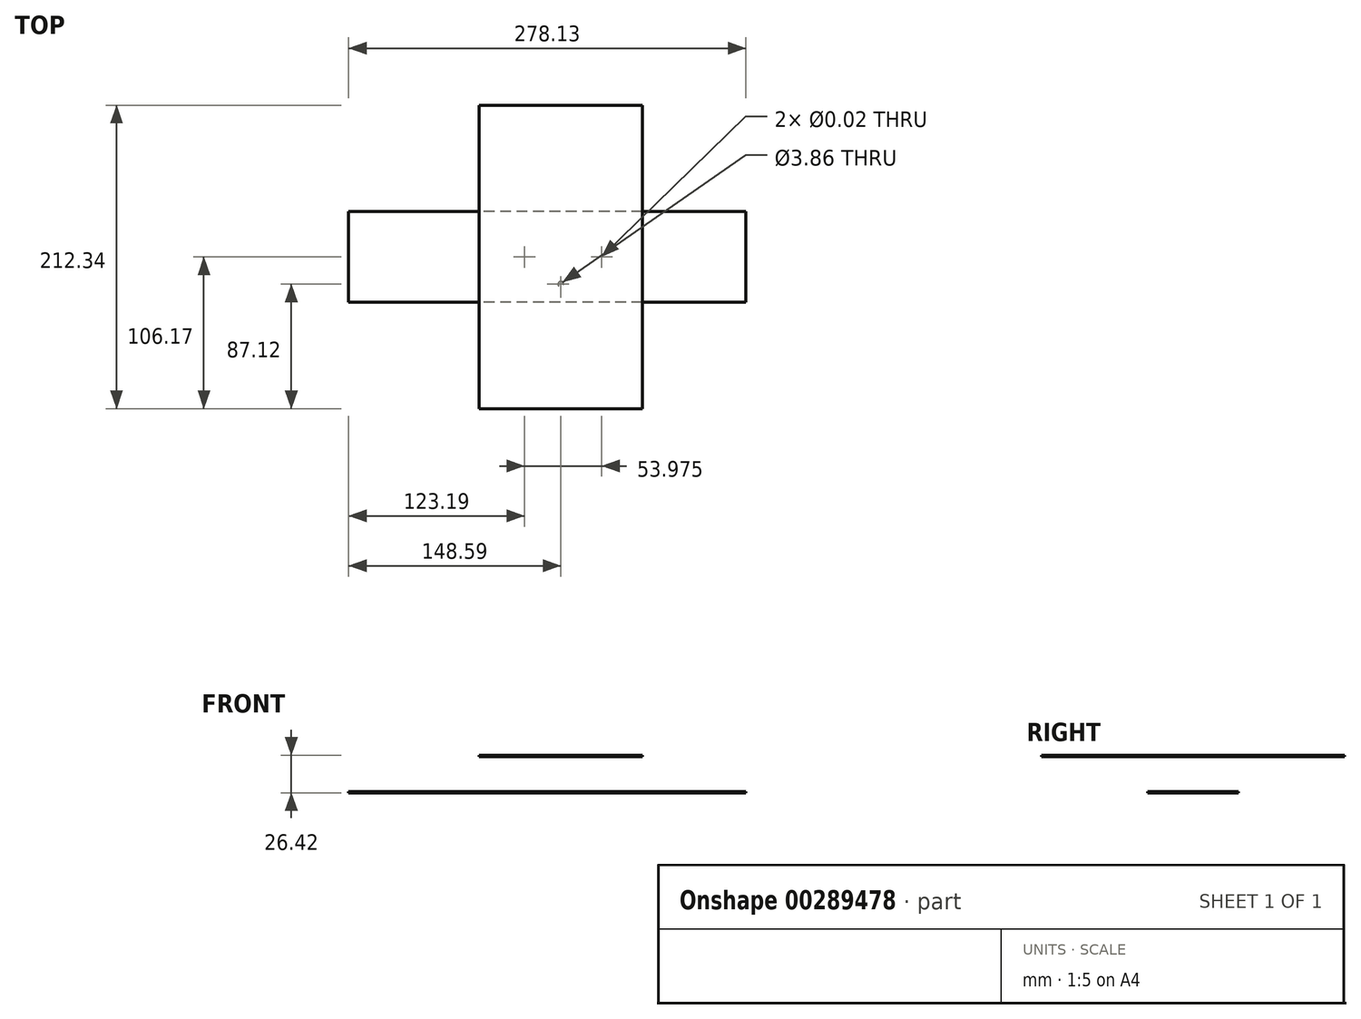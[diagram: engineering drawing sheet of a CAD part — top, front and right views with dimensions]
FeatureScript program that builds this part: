
annotation { "Feature Type Name" : "Feature", "Feature Type Description" : "" }
export const myFeature = defineFeature(function(context is Context, id is Id, definition is map)
    precondition{}
    {
        {
            var Q0;
            Q0=qCreatedBy(makeId("Top.planeOp"),FACE);
            var sketch = newSketch(context, id + "F0", { "sketchPlane" : qUnion([Q0])});
            skLineSegment(sketch, "E0.bottom", {"start": v(57.15, 31.75) * mm, "end": v(-57.15, 31.75) * mm});
            skLineSegment(sketch, "E0.top", {"start": v(57.15, -31.75) * mm, "end": v(-57.15, -31.75) * mm});
            skLineSegment(sketch, "E0.left", {"start": v(57.15, 31.75) * mm, "end": v(57.15, -31.75) * mm});
            skLineSegment(sketch, "E0.right", {"start": v(-57.15, 31.75) * mm, "end": v(-57.15, -31.75) * mm});
            skPoint(sketch, "E0.middle", {"position": v(0, 0) * mm});
            skLineSegment(sketch, "E1.bottom", {"start": v(57.15, 31.75) * mm, "end": v(97.8, 31.75) * mm});
            skLineSegment(sketch, "E1.top", {"start": v(57.15, -31.75) * mm, "end": v(97.8, -31.75) * mm});
            skLineSegment(sketch, "E1.right", {"start": v(97.8, 31.75) * mm, "end": v(97.8, -31.75) * mm});
            skLineSegment(sketch, "E2.bottom", {"start": v(97.8, 31.75) * mm, "end": v(129.54, 31.75) * mm});
            skLineSegment(sketch, "E2.top", {"start": v(97.8, -31.75) * mm, "end": v(129.54, -31.75) * mm});
            skLineSegment(sketch, "E2.right", {"start": v(129.54, 31.75) * mm, "end": v(129.54, -31.75) * mm});
            skLineSegment(sketch, "E3.bottom", {"start": v(-57.15, -31.75) * mm, "end": v(57.15, -31.75) * mm});
            skLineSegment(sketch, "E3.top", {"start": v(-57.15, -74.42) * mm, "end": v(57.15, -74.42) * mm});
            skLineSegment(sketch, "E3.left", {"start": v(-57.15, -31.75) * mm, "end": v(-57.15, -74.42) * mm});
            skLineSegment(sketch, "E3.right", {"start": v(57.15, -31.75) * mm, "end": v(57.15, -74.42) * mm});
            skLineSegment(sketch, "E4.top", {"start": v(-57.15, -106.17) * mm, "end": v(57.15, -106.17) * mm});
            skLineSegment(sketch, "E4.left", {"start": v(-57.15, -74.42) * mm, "end": v(-57.15, -106.17) * mm});
            skLineSegment(sketch, "E4.right", {"start": v(57.15, -74.42) * mm, "end": v(57.15, -106.17) * mm});
            skLineSegment(sketch, "E5.MirrorCS", {"start": v(-57.15, 31.75) * mm, "end": v(-97.8, 31.75) * mm});
            skLineSegment(sketch, "E6.MirrorCS", {"start": v(-57.15, -31.75) * mm, "end": v(-97.8, -31.75) * mm});
            skLineSegment(sketch, "E7.MirrorCS", {"start": v(-97.8, 31.75) * mm, "end": v(-97.8, -31.75) * mm});
            skLineSegment(sketch, "E8.MirrorCS", {"start": v(57.15, 74.42) * mm, "end": v(57.15, 106.17) * mm});
            skLineSegment(sketch, "E9.MirrorCS", {"start": v(-57.15, 74.42) * mm, "end": v(-57.15, 106.17) * mm});
            skLineSegment(sketch, "E10.MirrorCS", {"start": v(-57.15, 106.17) * mm, "end": v(57.15, 106.17) * mm});
            skLineSegment(sketch, "E11", {"start": v(-57.15, 74.42) * mm, "end": v(57.15, 74.42) * mm});
            skLineSegment(sketch, "E12.bottom", {"start": v(-97.8, 31.75) * mm, "end": v(-148.6, 31.75) * mm});
            skLineSegment(sketch, "E12.top", {"start": v(-97.8, -31.75) * mm, "end": v(-148.6, -31.75) * mm});
            skLineSegment(sketch, "E12.right", {"start": v(-148.6, 31.75) * mm, "end": v(-148.6, -31.75) * mm});
            skLineSegment(sketch, "E13", {"start": v(0, 0) * mm, "end": v(57.15, 0) * mm, "construction": true});
            skPoint(sketch, "E14", {"position": v(28.58, 0) * mm});
            skLineSegment(sketch, "E15", {"start": v(0, 0) * mm, "end": v(-57.15, 0) * mm, "construction": true});
            skPoint(sketch, "E16", {"position": v(-28.58, 0) * mm});
            skPoint(sketch, "E17", {"position": v(-25.4, 0) * mm});
            skPoint(sketch, "E18", {"position": v(0, -19.05) * mm});
            skLineSegment(sketch, "E19", {"start": v(57.15, 31.75) * mm, "end": v(57.15, 32.77) * mm});
            skLineSegment(sketch, "E20", {"start": v(57.15, 32.77) * mm, "end": v(57.15, 74.42) * mm});
            skLineSegment(sketch, "E21", {"start": v(-57.15, 31.75) * mm, "end": v(-57.15, 32.77) * mm});
            skLineSegment(sketch, "E22", {"start": v(-57.15, 32.77) * mm, "end": v(-57.15, 74.42) * mm});
            skPoint(sketch, "E23", {"position": v(-57.15, -32.77) * mm});
            skPoint(sketch, "E24", {"position": v(57.15, -32.77) * mm});
            skPoint(sketch, "E25", {"position": v(57.15, 31.75) * mm});
            skSolve(sketch);
        }
        {
            var Q0;
            Q0=makeQuery(id+"F0.imprint","IMPRINT",FACE,{"disambiguationData":[TD([[makeQuery(id+"F0.imprint","IMPRINT",EDGE,{"derivedFrom":sQuery(id+"F0.wireOp",EDGE,"E0.bottom")}),1.0]])]});
            var Q1;
            Q1=makeQuery(id+"F0.imprint","IMPRINT",FACE,{"disambiguationData":[TD([[makeQuery(id+"F0.imprint","IMPRINT",EDGE,{"derivedFrom":sQuery(id+"F0.wireOp",EDGE,"E0.right")}),-1.0]])]});
            var Q2;
            Q2=makeQuery(id+"F0.imprint","IMPRINT",FACE,{"disambiguationData":[TD([[makeQuery(id+"F0.imprint","IMPRINT",EDGE,{"derivedFrom":sQuery(id+"F0.wireOp",EDGE,"E12.bottom")}),1.0]])]});
            var Q3;
            Q3=makeQuery(id+"F0.imprint","IMPRINT",FACE,{"disambiguationData":[TD([[makeQuery(id+"F0.imprint","IMPRINT",EDGE,{"derivedFrom":sQuery(id+"F0.wireOp",EDGE,"E1.bottom")}),-1.0]])]});
            var Q4;
            Q4=makeQuery(id+"F0.imprint","IMPRINT",FACE,{"disambiguationData":[TD([[makeQuery(id+"F0.imprint","IMPRINT",EDGE,{"derivedFrom":sQuery(id+"F0.wireOp",EDGE,"E2.bottom")}),-1.0]])]});
            extrude(context, id + "F1", {"entities" : qUnion([Q0, Q1, Q2, Q3, Q4]), "depth" : 1.02 * mm});
        }
        {
            var Q0;
            Q0=makeQuery(id+"F1.opExtrude","CAP_FACE",FACE,{"disambiguationData":[OSD([sQuery(id+"F0.wireOp",EDGE,"E1.bottom"),sQuery(id+"F0.wireOp",EDGE,"E1.top"),sQuery(id+"F0.wireOp",EDGE,"E2.bottom"),sQuery(id+"F0.wireOp",EDGE,"E2.top"),sQuery(id+"F0.wireOp",EDGE,"E2.right"),sQuery(id+"F0.wireOp",EDGE,"E3.left"),sQuery(id+"F0.wireOp",EDGE,"E3.right"),sQuery(id+"F0.wireOp",EDGE,"E4.top"),sQuery(id+"F0.wireOp",EDGE,"E4.left"),sQuery(id+"F0.wireOp",EDGE,"E4.right"),sQuery(id+"F0.wireOp",EDGE,"E5.MirrorCS"),sQuery(id+"F0.wireOp",EDGE,"E6.MirrorCS"),sQuery(id+"F0.wireOp",EDGE,"37d40448-32c7-41bc-b376-fd8bdd51f9650.MirrorCS"),sQuery(id+"F0.wireOp",EDGE,"85dccc23-6113-4114-afa1-5dd2b9facbff0.MirrorCS"),sQuery(id+"F0.wireOp",EDGE,"86545dad-6d07-494b-aa5d-beba49be264a0.MirrorCS"),sQuery(id+"F0.wireOp",EDGE,"13e9073a-3274-4a79-9c35-b42b4b046fd70.MirrorCS"),sQuery(id+"F0.wireOp",EDGE,"17af86ea-e885-4359-adf6-516d9f65ff840.MirrorCS"),sQuery(id+"F0.wireOp",EDGE,"E8.MirrorCS"),sQuery(id+"F0.wireOp",EDGE,"E9.MirrorCS"),sQuery(id+"F0.wireOp",EDGE,"E10.MirrorCS")])],"isStart":false});
            var sketch = newSketch(context, id + "F2", { "sketchPlane" : qUnion([Q0])});
            skPoint(sketch, "E26.0", {"position": v(57.15, 74.42) * mm});
            skPoint(sketch, "E27.0", {"position": v(-57.15, 72.4) * mm});
            skPoint(sketch, "E28.0", {"position": v(-97.8, 31.75) * mm});
            skPoint(sketch, "E29.0", {"position": v(-97.8, -31.75) * mm});
            skPoint(sketch, "E30.0", {"position": v(-57.15, -74.42) * mm});
            skPoint(sketch, "E31.0", {"position": v(57.15, -74.42) * mm});
            skPoint(sketch, "E32.0", {"position": v(97.8, -31.75) * mm});
            skPoint(sketch, "E33.0", {"position": v(97.8, 31.75) * mm});
            skSolve(sketch);
        }
        {
            var Q0;
            Q0=sQuery(id+"F2.wireOp",VERTEX,"E27.0");
            var Q1;
            Q1=sQuery(id+"F2.wireOp",VERTEX,"E26.0");
            var Q2;
            Q2=sQuery(id+"F2.wireOp",VERTEX,"E33.0");
            var Q3;
            Q3=sQuery(id+"F2.wireOp",VERTEX,"E32.0");
            var Q4;
            Q4=sQuery(id+"F2.wireOp",VERTEX,"E31.0");
            var Q5;
            Q5=sQuery(id+"F2.wireOp",VERTEX,"E30.0");
            var Q6;
            Q6=sQuery(id+"F2.wireOp",VERTEX,"E29.0");
            var Q7;
            Q7=sQuery(id+"F2.wireOp",VERTEX,"E28.0");
            var Q8;
            Q8=makeQuery(id+"F1.opExtrude","SWEPT_BODY",BODY,{"disambiguationData":[OSD([sQuery(id+"F0.wireOp",EDGE,"E1.bottom"),sQuery(id+"F0.wireOp",EDGE,"E1.top"),sQuery(id+"F0.wireOp",EDGE,"E2.bottom"),sQuery(id+"F0.wireOp",EDGE,"E2.top"),sQuery(id+"F0.wireOp",EDGE,"E2.right"),sQuery(id+"F0.wireOp",EDGE,"E3.left"),sQuery(id+"F0.wireOp",EDGE,"E3.right"),sQuery(id+"F0.wireOp",EDGE,"E4.top"),sQuery(id+"F0.wireOp",EDGE,"E4.left"),sQuery(id+"F0.wireOp",EDGE,"E4.right"),sQuery(id+"F0.wireOp",EDGE,"E5.MirrorCS"),sQuery(id+"F0.wireOp",EDGE,"E6.MirrorCS"),sQuery(id+"F0.wireOp",EDGE,"37d40448-32c7-41bc-b376-fd8bdd51f9650.MirrorCS"),sQuery(id+"F0.wireOp",EDGE,"85dccc23-6113-4114-afa1-5dd2b9facbff0.MirrorCS"),sQuery(id+"F0.wireOp",EDGE,"86545dad-6d07-494b-aa5d-beba49be264a0.MirrorCS"),sQuery(id+"F0.wireOp",EDGE,"13e9073a-3274-4a79-9c35-b42b4b046fd70.MirrorCS"),sQuery(id+"F0.wireOp",EDGE,"17af86ea-e885-4359-adf6-516d9f65ff840.MirrorCS"),sQuery(id+"F0.wireOp",EDGE,"E8.MirrorCS"),sQuery(id+"F0.wireOp",EDGE,"E9.MirrorCS"),sQuery(id+"F0.wireOp",EDGE,"E10.MirrorCS")])]});
            hole(context, id + "F3", {"style" : HoleStyle.SIMPLE, "endStyle" : HoleEndStyle.THROUGH, "holeDiameter" : 0.13 * mm, "tappedDepth" : 12.7 * mm, "tapClearance" : 3, "locations" : qUnion([Q0, Q1, Q2, Q3, Q4, Q5, Q6, Q7]), "scope" : qUnion([Q8]), "startStyle" : HoleStartStyle.PART});
        }
        {
            var Q0;
            Q0=sQuery(id+"F0.wireOp",VERTEX,"E5.MirrorCS.start");
            var Q1;
            Q1=sQuery(id+"F0.wireOp",VERTEX,"E3.bottom.end");
            var Q2;
            Q2=sQuery(id+"F0.wireOp",VERTEX,"E25");
            var Q3;
            Q3=sQuery(id+"F0.wireOp",VERTEX,"E3.bottom.start");
            var Q4;
            Q4=makeQuery(id+"F1.opExtrude","SWEPT_BODY",BODY,{"disambiguationData":[OSD([sQuery(id+"F0.wireOp",EDGE,"E1.bottom"),sQuery(id+"F0.wireOp",EDGE,"E1.top"),sQuery(id+"F0.wireOp",EDGE,"E2.bottom"),sQuery(id+"F0.wireOp",EDGE,"E2.top"),sQuery(id+"F0.wireOp",EDGE,"E2.right"),sQuery(id+"F0.wireOp",EDGE,"E3.left"),sQuery(id+"F0.wireOp",EDGE,"E3.right"),sQuery(id+"F0.wireOp",EDGE,"E4.top"),sQuery(id+"F0.wireOp",EDGE,"E4.left"),sQuery(id+"F0.wireOp",EDGE,"E4.right"),sQuery(id+"F0.wireOp",EDGE,"E5.MirrorCS"),sQuery(id+"F0.wireOp",EDGE,"E6.MirrorCS"),sQuery(id+"F0.wireOp",EDGE,"37d40448-32c7-41bc-b376-fd8bdd51f9650.MirrorCS"),sQuery(id+"F0.wireOp",EDGE,"85dccc23-6113-4114-afa1-5dd2b9facbff0.MirrorCS"),sQuery(id+"F0.wireOp",EDGE,"86545dad-6d07-494b-aa5d-beba49be264a0.MirrorCS"),sQuery(id+"F0.wireOp",EDGE,"13e9073a-3274-4a79-9c35-b42b4b046fd70.MirrorCS"),sQuery(id+"F0.wireOp",EDGE,"17af86ea-e885-4359-adf6-516d9f65ff840.MirrorCS"),sQuery(id+"F0.wireOp",EDGE,"E8.MirrorCS"),sQuery(id+"F0.wireOp",EDGE,"E9.MirrorCS"),sQuery(id+"F0.wireOp",EDGE,"E10.MirrorCS")])]});
            hole(context, id + "F4", {"style" : HoleStyle.SIMPLE, "endStyle" : HoleEndStyle.THROUGH, "oppositeDirection" : true, "holeDiameter" : 0.13 * mm, "tappedDepth" : 12.7 * mm, "tapClearance" : 3, "locations" : qUnion([Q0, Q1, Q2, Q3]), "scope" : qUnion([Q4]), "startStyle" : HoleStartStyle.PART});
        }
        {
            var Q0;
            Q0=sQuery(id+"F0.wireOp",VERTEX,"E17");
            var Q1;
            Q1=makeQuery(id+"F1.opExtrude","SWEPT_BODY",BODY,{"disambiguationData":[OSD([sQuery(id+"F0.wireOp",EDGE,"E1.bottom"),sQuery(id+"F0.wireOp",EDGE,"E1.top"),sQuery(id+"F0.wireOp",EDGE,"E2.bottom"),sQuery(id+"F0.wireOp",EDGE,"E2.top"),sQuery(id+"F0.wireOp",EDGE,"E2.right"),sQuery(id+"F0.wireOp",EDGE,"E3.left"),sQuery(id+"F0.wireOp",EDGE,"E3.right"),sQuery(id+"F0.wireOp",EDGE,"E4.top"),sQuery(id+"F0.wireOp",EDGE,"E4.left"),sQuery(id+"F0.wireOp",EDGE,"E4.right"),sQuery(id+"F0.wireOp",EDGE,"E5.MirrorCS"),sQuery(id+"F0.wireOp",EDGE,"E6.MirrorCS"),sQuery(id+"F0.wireOp",EDGE,"13e9073a-3274-4a79-9c35-b42b4b046fd70.MirrorCS"),sQuery(id+"F0.wireOp",EDGE,"17af86ea-e885-4359-adf6-516d9f65ff840.MirrorCS"),sQuery(id+"F0.wireOp",EDGE,"E8.MirrorCS"),sQuery(id+"F0.wireOp",EDGE,"E9.MirrorCS"),sQuery(id+"F0.wireOp",EDGE,"E10.MirrorCS"),sQuery(id+"F0.wireOp",EDGE,"E12.bottom"),sQuery(id+"F0.wireOp",EDGE,"E12.top"),sQuery(id+"F0.wireOp",EDGE,"E12.right")])]});
            hole(context, id + "F5", {"style" : HoleStyle.SIMPLE, "endStyle" : HoleEndStyle.THROUGH, "oppositeDirection" : true, "standardTappedOrClearance" : lookupTablePath({ "standard" : "ANSI", "size" : "9/16 (0.56)", "type" : "Drilled" }), "standardBlindInLast" : lookupTablePath({ "standard" : "ANSI", "size" : "9/16 (0.56)", "type" : "Drilled" }), "holeDiameter" : 9 / 406.4 * mm, "majorDiameter" : 6.35 * mm, "tappedDepth" : 12.7 * mm, "tapClearance" : 3, "locations" : qUnion([Q0]), "scope" : qUnion([Q1]), "startStyle" : HoleStartStyle.PART});
        }
        {
            var Q0;
            Q0=sQuery(id+"F0.wireOp",VERTEX,"E14");
            var Q1;
            Q1=makeQuery(id+"F1.opExtrude","SWEPT_BODY",BODY,{"disambiguationData":[OSD([sQuery(id+"F0.wireOp",EDGE,"E1.bottom"),sQuery(id+"F0.wireOp",EDGE,"E1.top"),sQuery(id+"F0.wireOp",EDGE,"E2.bottom"),sQuery(id+"F0.wireOp",EDGE,"E2.top"),sQuery(id+"F0.wireOp",EDGE,"E2.right"),sQuery(id+"F0.wireOp",EDGE,"E3.left"),sQuery(id+"F0.wireOp",EDGE,"E3.right"),sQuery(id+"F0.wireOp",EDGE,"E4.top"),sQuery(id+"F0.wireOp",EDGE,"E4.left"),sQuery(id+"F0.wireOp",EDGE,"E4.right"),sQuery(id+"F0.wireOp",EDGE,"E5.MirrorCS"),sQuery(id+"F0.wireOp",EDGE,"E6.MirrorCS"),sQuery(id+"F0.wireOp",EDGE,"13e9073a-3274-4a79-9c35-b42b4b046fd70.MirrorCS"),sQuery(id+"F0.wireOp",EDGE,"17af86ea-e885-4359-adf6-516d9f65ff840.MirrorCS"),sQuery(id+"F0.wireOp",EDGE,"E8.MirrorCS"),sQuery(id+"F0.wireOp",EDGE,"E9.MirrorCS"),sQuery(id+"F0.wireOp",EDGE,"E10.MirrorCS"),sQuery(id+"F0.wireOp",EDGE,"E12.bottom"),sQuery(id+"F0.wireOp",EDGE,"E12.top"),sQuery(id+"F0.wireOp",EDGE,"E12.right")])]});
            hole(context, id + "F6", {"style" : HoleStyle.SIMPLE, "endStyle" : HoleEndStyle.THROUGH, "oppositeDirection" : true, "standardTappedOrClearance" : lookupTablePath({ "standard" : "ANSI", "size" : "7/16 (0.44)", "type" : "Drilled" }), "standardBlindInLast" : lookupTablePath({ "standard" : "ANSI", "size" : "7/16 (0.44)", "type" : "Drilled" }), "holeDiameter" : 7 / 406.4 * mm, "majorDiameter" : 6.35 * mm, "tappedDepth" : 12.7 * mm, "tapClearance" : 3, "locations" : qUnion([Q0]), "scope" : qUnion([Q1]), "startStyle" : HoleStartStyle.PART});
        }
        {
            var Q0;
            Q0=sQuery(id+"F0.wireOp",VERTEX,"E18");
            var Q1;
            Q1=makeQuery(id+"F1.opExtrude","SWEPT_BODY",BODY,{"disambiguationData":[OSD([sQuery(id+"F0.wireOp",EDGE,"E1.bottom"),sQuery(id+"F0.wireOp",EDGE,"E1.top"),sQuery(id+"F0.wireOp",EDGE,"E2.bottom"),sQuery(id+"F0.wireOp",EDGE,"E2.top"),sQuery(id+"F0.wireOp",EDGE,"E2.right"),sQuery(id+"F0.wireOp",EDGE,"E3.left"),sQuery(id+"F0.wireOp",EDGE,"E3.right"),sQuery(id+"F0.wireOp",EDGE,"E4.top"),sQuery(id+"F0.wireOp",EDGE,"E4.left"),sQuery(id+"F0.wireOp",EDGE,"E4.right"),sQuery(id+"F0.wireOp",EDGE,"E5.MirrorCS"),sQuery(id+"F0.wireOp",EDGE,"E6.MirrorCS"),sQuery(id+"F0.wireOp",EDGE,"13e9073a-3274-4a79-9c35-b42b4b046fd70.MirrorCS"),sQuery(id+"F0.wireOp",EDGE,"17af86ea-e885-4359-adf6-516d9f65ff840.MirrorCS"),sQuery(id+"F0.wireOp",EDGE,"E8.MirrorCS"),sQuery(id+"F0.wireOp",EDGE,"E9.MirrorCS"),sQuery(id+"F0.wireOp",EDGE,"E10.MirrorCS"),sQuery(id+"F0.wireOp",EDGE,"E12.bottom"),sQuery(id+"F0.wireOp",EDGE,"E12.top"),sQuery(id+"F0.wireOp",EDGE,"E12.right")])]});
            hole(context, id + "F7", {"style" : HoleStyle.SIMPLE, "endStyle" : HoleEndStyle.THROUGH, "oppositeDirection" : true, "standardTappedOrClearance" : lookupTablePath({ "standard" : "ANSI", "size" : "#24 (0.15)", "type" : "Drilled" }), "standardBlindInLast" : lookupTablePath({ "standard" : "ANSI", "size" : "#24 (0.15)", "type" : "Drilled" }), "holeDiameter" : 3.86 * mm, "majorDiameter" : 6.35 * mm, "tappedDepth" : 12.7 * mm, "tapClearance" : 3, "locations" : qUnion([Q0]), "scope" : qUnion([Q1]), "startStyle" : HoleStartStyle.PART});
        }
        {
            var Q0;
            Q0=qCreatedBy(makeId("Top.planeOp"),FACE);
            cPlane(context, id + "F8", {"entities" : qUnion([Q0]), "cplaneType" : CPlaneType.OFFSET, "offset" : 25.4 * mm, "width" : 152.4 * mm, "height" : 152.4 * mm});
        }
        {
            var Q0;
            Q0=qCreatedBy(id+"F8.planeOp",FACE);
            var sketch = newSketch(context, id + "F9", { "sketchPlane" : qUnion([Q0])});
            skLineSegment(sketch, "E34.0.0", {"start": v(-57.15, 106.17) * mm, "end": v(-57.15, 74.42) * mm});
            skLineSegment(sketch, "E34.0.1", {"start": v(-57.15, 74.42) * mm, "end": v(57.15, 74.42) * mm});
            skLineSegment(sketch, "E34.0.2", {"start": v(57.15, 74.42) * mm, "end": v(57.15, 106.17) * mm});
            skLineSegment(sketch, "E34.0.3", {"start": v(57.15, 106.17) * mm, "end": v(-57.15, 106.17) * mm});
            skLineSegment(sketch, "E35.0.0", {"start": v(-57.15, 74.42) * mm, "end": v(-57.15, 32.77) * mm});
            skLineSegment(sketch, "E35.0.1", {"start": v(-57.15, 32.77) * mm, "end": v(-57.15, 31.75) * mm});
            skLineSegment(sketch, "E35.0.2", {"start": v(-57.15, 31.75) * mm, "end": v(57.15, 31.75) * mm});
            skLineSegment(sketch, "E35.0.3", {"start": v(57.15, 31.75) * mm, "end": v(57.15, 32.77) * mm});
            skLineSegment(sketch, "E35.0.4", {"start": v(57.15, 32.77) * mm, "end": v(57.15, 74.42) * mm});
            skLineSegment(sketch, "E35.0.5", {"start": v(57.15, 74.42) * mm, "end": v(-57.15, 74.42) * mm});
            skLineSegment(sketch, "E36.0.0", {"start": v(57.15, -74.42) * mm, "end": v(57.15, -31.75) * mm});
            skLineSegment(sketch, "E36.0.1", {"start": v(57.15, -31.75) * mm, "end": v(-57.15, -31.75) * mm});
            skLineSegment(sketch, "E36.0.2", {"start": v(-57.15, -31.75) * mm, "end": v(-57.15, -74.42) * mm});
            skLineSegment(sketch, "E36.0.3", {"start": v(-57.15, -74.42) * mm, "end": v(57.15, -74.42) * mm});
            skLineSegment(sketch, "E37.0.0", {"start": v(57.15, -74.42) * mm, "end": v(-57.15, -74.42) * mm});
            skLineSegment(sketch, "E37.0.1", {"start": v(-57.15, -74.42) * mm, "end": v(-57.15, -106.17) * mm});
            skLineSegment(sketch, "E37.0.2", {"start": v(-57.15, -106.17) * mm, "end": v(57.15, -106.17) * mm});
            skLineSegment(sketch, "E37.0.3", {"start": v(57.15, -106.17) * mm, "end": v(57.15, -74.42) * mm});
            skLineSegment(sketch, "E38.0.0", {"start": v(-57.15, -31.75) * mm, "end": v(57.15, -31.75) * mm});
            skLineSegment(sketch, "E38.0.1", {"start": v(57.15, -31.75) * mm, "end": v(57.15, 31.75) * mm});
            skLineSegment(sketch, "E38.0.2", {"start": v(57.15, 31.75) * mm, "end": v(-57.15, 31.75) * mm});
            skLineSegment(sketch, "E38.0.3", {"start": v(-57.15, 31.75) * mm, "end": v(-57.15, -31.75) * mm});
            skPoint(sketch, "E39.0", {"position": v(57.15, -32.77) * mm});
            skPoint(sketch, "E40.0", {"position": v(-57.15, -32.77) * mm});
            skSolve(sketch);
        }
        {
            var Q0;
            Q0 = qSketchRegion(id + "F9", true);
            extrude(context, id + "F10", {"entities" : qUnion([Q0]), "depth" : 1.02 * mm});
        }
        {
            var Q0;
            Q0=sQuery(id+"F9.wireOp",VERTEX,"E35.0.5.end");
            var Q1;
            Q1=sQuery(id+"F9.wireOp",VERTEX,"E35.0.4.end");
            var Q2;
            Q2=sQuery(id+"F9.wireOp",VERTEX,"E35.0.4.start");
            var Q3;
            Q3=sQuery(id+"F9.wireOp",VERTEX,"E35.0.0.end");
            var Q4;
            Q4=sQuery(id+"F9.wireOp",VERTEX,"E40.0");
            var Q5;
            Q5=sQuery(id+"F9.wireOp",VERTEX,"E39.0");
            var Q6;
            Q6=sQuery(id+"F9.wireOp",VERTEX,"E36.0.2.end");
            var Q7;
            Q7=sQuery(id+"F9.wireOp",VERTEX,"E37.0.0.start");
            var Q8;
            Q8=makeQuery(id+"F10.opExtrude","SWEPT_BODY",BODY,{"disambiguationData":[OSD([sQuery(id+"F9.wireOp",EDGE,"E34.0.0"),sQuery(id+"F9.wireOp",EDGE,"E34.0.2"),sQuery(id+"F9.wireOp",EDGE,"E34.0.3"),sQuery(id+"F9.wireOp",EDGE,"E35.0.0"),sQuery(id+"F9.wireOp",EDGE,"E35.0.1"),sQuery(id+"F9.wireOp",EDGE,"E35.0.3"),sQuery(id+"F9.wireOp",EDGE,"E35.0.4"),sQuery(id+"F9.wireOp",EDGE,"E36.0.0"),sQuery(id+"F9.wireOp",EDGE,"E36.0.2"),sQuery(id+"F9.wireOp",EDGE,"E37.0.1"),sQuery(id+"F9.wireOp",EDGE,"E37.0.2"),sQuery(id+"F9.wireOp",EDGE,"E37.0.3"),sQuery(id+"F9.wireOp",EDGE,"E38.0.1"),sQuery(id+"F9.wireOp",EDGE,"E38.0.3")])]});
            hole(context, id + "F11", {"style" : HoleStyle.SIMPLE, "endStyle" : HoleEndStyle.THROUGH, "oppositeDirection" : true, "holeDiameter" : 0.13 * mm, "tappedDepth" : 12.7 * mm, "tapClearance" : 3, "locations" : qUnion([Q0, Q1, Q2, Q3, Q4, Q5, Q6, Q7]), "scope" : qUnion([Q8]), "startStyle" : HoleStartStyle.PART});
        }
    });
